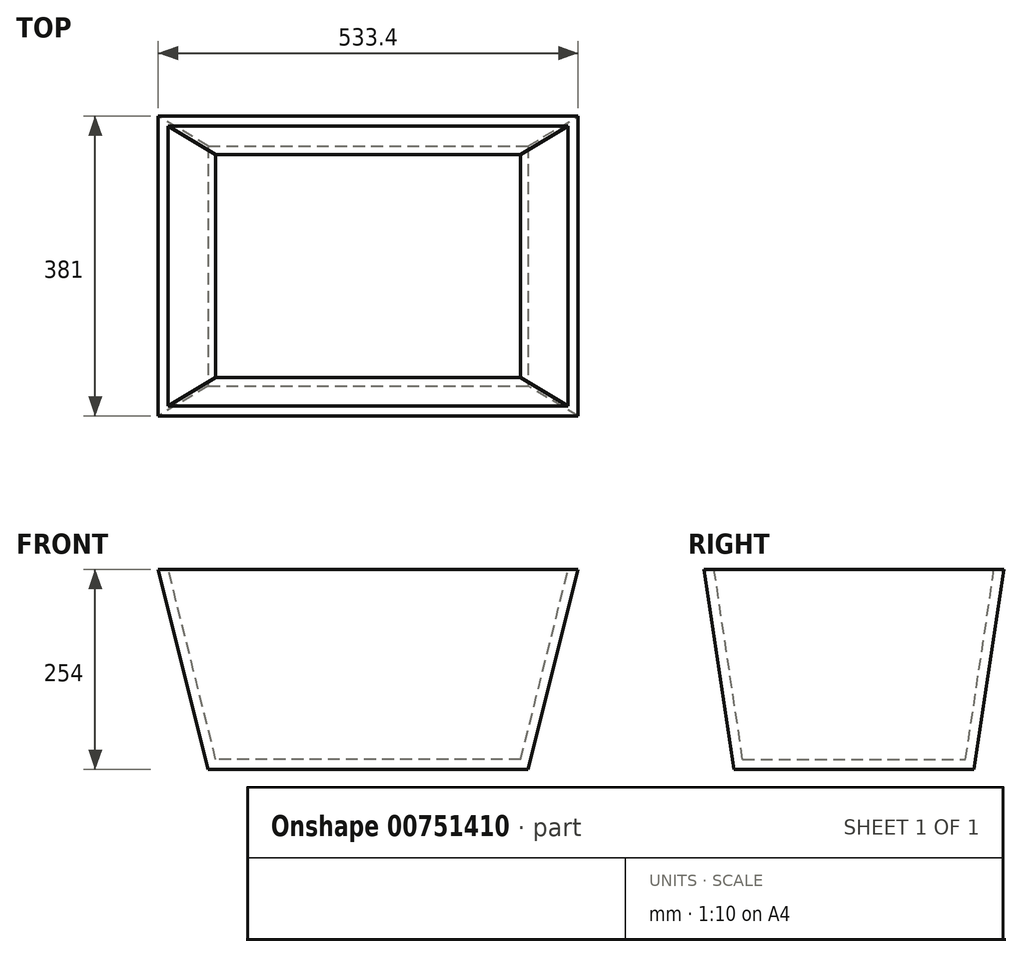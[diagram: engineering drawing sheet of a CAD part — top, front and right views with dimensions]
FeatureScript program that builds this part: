
annotation { "Feature Type Name" : "Feature", "Feature Type Description" : "" }
export const myFeature = defineFeature(function(context is Context, id is Id, definition is map)
    precondition{}
    {
        {
            var Q0;
            Q0=qCreatedBy(makeId("Top.planeOp"),FACE);
            var sketch = newSketch(context, id + "F0", { "sketchPlane" : qUnion([Q0])});
            skLineSegment(sketch, "E0.bottom", {"start": v(-203.2, 152.4) * mm, "end": v(203.2, 152.4) * mm});
            skLineSegment(sketch, "E0.top", {"start": v(-203.2, -152.4) * mm, "end": v(203.2, -152.4) * mm});
            skLineSegment(sketch, "E0.left", {"start": v(-203.2, 152.4) * mm, "end": v(-203.2, -152.4) * mm});
            skLineSegment(sketch, "E0.right", {"start": v(203.2, 152.4) * mm, "end": v(203.2, -152.4) * mm});
            skLineSegment(sketch, "E1", {"start": v(-203.2, 152.4) * mm, "end": v(203.2, -152.4) * mm, "construction": true});
            skLineSegment(sketch, "E2", {"start": v(203.2, 152.4) * mm, "end": v(-203.2, -152.4) * mm, "construction": true});
            skPoint(sketch, "E3", {"position": v(0, 0) * mm});
            skLineSegment(sketch, "E4.0", {"start": v(-190.5, 139.7) * mm, "end": v(190.5, 139.7) * mm});
            skLineSegment(sketch, "E4.1", {"start": v(-190.5, 139.7) * mm, "end": v(-190.5, -139.7) * mm});
            skLineSegment(sketch, "E4.2", {"start": v(-190.5, -139.7) * mm, "end": v(190.5, -139.7) * mm});
            skLineSegment(sketch, "E4.3", {"start": v(190.5, 139.7) * mm, "end": v(190.5, -139.7) * mm});
            skLineSegment(sketch, "E5", {"start": v(-190.5, 139.7) * mm, "end": v(-203.2, 152.4) * mm});
            skLineSegment(sketch, "E6", {"start": v(190.5, 139.7) * mm, "end": v(203.2, 152.4) * mm});
            skLineSegment(sketch, "E7", {"start": v(203.2, -152.4) * mm, "end": v(190.5, -139.7) * mm});
            skLineSegment(sketch, "E8", {"start": v(-190.5, -139.7) * mm, "end": v(-203.2, -152.4) * mm});
            skSolve(sketch);
        }
        {
            var Q0;
            Q0=qCreatedBy(makeId("Top.planeOp"),FACE);
            cPlane(context, id + "F1", {"entities" : qUnion([Q0]), "cplaneType" : CPlaneType.OFFSET, "offset" : 254 * mm, "width" : 152.4 * mm, "height" : 152.4 * mm});
        }
        {
            var Q0;
            Q0=qCreatedBy(id+"F1.planeOp",FACE);
            var sketch = newSketch(context, id + "F2", { "sketchPlane" : qUnion([Q0])});
            skLineSegment(sketch, "E9.bottom", {"start": v(-266.7, 190.5) * mm, "end": v(266.7, 190.5) * mm});
            skLineSegment(sketch, "E9.top", {"start": v(-266.7, -190.5) * mm, "end": v(266.7, -190.5) * mm});
            skLineSegment(sketch, "E9.left", {"start": v(-266.7, 190.5) * mm, "end": v(-266.7, -190.5) * mm});
            skLineSegment(sketch, "E9.right", {"start": v(266.7, 190.5) * mm, "end": v(266.7, -190.5) * mm});
            skLineSegment(sketch, "E10", {"start": v(-266.7, 190.5) * mm, "end": v(266.7, -190.5) * mm, "construction": true});
            skLineSegment(sketch, "E11", {"start": v(266.7, 190.5) * mm, "end": v(-266.7, -190.5) * mm, "construction": true});
            skPoint(sketch, "E12", {"position": v(0, 0) * mm});
            skLineSegment(sketch, "E13.0", {"start": v(-254, 177.8) * mm, "end": v(254, 177.8) * mm});
            skLineSegment(sketch, "E13.1", {"start": v(-254, 177.8) * mm, "end": v(-254, -177.8) * mm});
            skLineSegment(sketch, "E13.2", {"start": v(-254, -177.8) * mm, "end": v(254, -177.8) * mm});
            skLineSegment(sketch, "E13.3", {"start": v(254, 177.8) * mm, "end": v(254, -177.8) * mm});
            skLineSegment(sketch, "E14", {"start": v(-254, 177.8) * mm, "end": v(-266.7, 190.5) * mm});
            skLineSegment(sketch, "E15", {"start": v(254, 177.8) * mm, "end": v(266.7, 190.5) * mm});
            skLineSegment(sketch, "E16", {"start": v(266.7, -190.5) * mm, "end": v(254, -177.8) * mm});
            skLineSegment(sketch, "E17", {"start": v(-254, -177.8) * mm, "end": v(-266.7, -190.5) * mm});
            skSolve(sketch);
        }
        {
            var Q0;
            Q0=makeQuery(id+"F0.imprint","IMPRINT",FACE,{"disambiguationData":[TD([[makeQuery(id+"F0.imprint","IMPRINT",EDGE,{"derivedFrom":sQuery(id+"F0.wireOp",EDGE,"E0.bottom")}),-1.0]])]});
            var Q1;
            Q1=makeQuery(id+"F2.imprint","IMPRINT",FACE,{"disambiguationData":[TD([[makeQuery(id+"F2.imprint","IMPRINT",EDGE,{"derivedFrom":sQuery(id+"F2.wireOp",EDGE,"E9.bottom")}),-1.0]])]});
            loft(context, id + "F3", {"sheetProfilesArray" : [{ "sheetProfileEntities" : qUnion([Q0]) }, { "sheetProfileEntities" : qUnion([Q1]) }]});
        }
        {
            var Q1;
            Q1=makeQuery(id+"F0.imprint","IMPRINT",FACE,{"disambiguationData":[TD([[makeQuery(id+"F0.imprint","IMPRINT",EDGE,{"derivedFrom":sQuery(id+"F0.wireOp",EDGE,"E0.left")}),1.0]])]});
            var Q2;
            Q2=makeQuery(id+"F2.imprint","IMPRINT",FACE,{"disambiguationData":[TD([[makeQuery(id+"F2.imprint","IMPRINT",EDGE,{"derivedFrom":sQuery(id+"F2.wireOp",EDGE,"E9.left")}),1.0]])]});
            loft(context, id + "F4", {"operationType" : NewBodyOperationType.ADD, "sheetProfilesArray" : [{ "sheetProfileEntities" : qUnion([Q1]) }, { "sheetProfileEntities" : qUnion([Q2]) }]});
        }
        {
            var Q1;
            Q1=makeQuery(id+"F2.imprint","IMPRINT",FACE,{"disambiguationData":[TD([[makeQuery(id+"F2.imprint","IMPRINT",EDGE,{"derivedFrom":sQuery(id+"F2.wireOp",EDGE,"E9.top")}),1.0]])]});
            var Q2;
            Q2=makeQuery(id+"F0.imprint","IMPRINT",FACE,{"disambiguationData":[TD([[makeQuery(id+"F0.imprint","IMPRINT",EDGE,{"derivedFrom":sQuery(id+"F0.wireOp",EDGE,"E0.top")}),1.0]])]});
            loft(context, id + "F5", {"operationType" : NewBodyOperationType.ADD, "sheetProfilesArray" : [{ "sheetProfileEntities" : qUnion([Q1]) }, { "sheetProfileEntities" : qUnion([Q2]) }]});
        }
        {
            var Q1;
            Q1=makeQuery(id+"F2.imprint","IMPRINT",FACE,{"disambiguationData":[TD([[makeQuery(id+"F2.imprint","IMPRINT",EDGE,{"derivedFrom":sQuery(id+"F2.wireOp",EDGE,"E9.right")}),-1.0]])]});
            var Q2;
            Q2=makeQuery(id+"F0.imprint","IMPRINT",FACE,{"disambiguationData":[TD([[makeQuery(id+"F0.imprint","IMPRINT",EDGE,{"derivedFrom":sQuery(id+"F0.wireOp",EDGE,"E0.right")}),-1.0]])]});
            loft(context, id + "F6", {"operationType" : NewBodyOperationType.ADD, "sheetProfilesArray" : [{ "sheetProfileEntities" : qUnion([Q1]) }, { "sheetProfileEntities" : qUnion([Q2]) }]});
        }
        {
            var Q0;
            Q0=makeQuery(id+"F0.imprint","IMPRINT",FACE,{"disambiguationData":[TD([[makeQuery(id+"F0.imprint","IMPRINT",EDGE,{"derivedFrom":sQuery(id+"F0.wireOp",EDGE,"E0.bottom")}),-1.0]])]});
            var Q1;
            Q1=makeQuery(id+"F0.imprint","IMPRINT",FACE,{"disambiguationData":[TD([[makeQuery(id+"F0.imprint","IMPRINT",EDGE,{"derivedFrom":sQuery(id+"F0.wireOp",EDGE,"E0.left")}),1.0]])]});
            var Q2;
            Q2=makeQuery(id+"F0.imprint","IMPRINT",FACE,{"disambiguationData":[TD([[makeQuery(id+"F0.imprint","IMPRINT",EDGE,{"derivedFrom":sQuery(id+"F0.wireOp",EDGE,"E0.top")}),1.0]])]});
            var Q3;
            Q3=makeQuery(id+"F0.imprint","IMPRINT",FACE,{"disambiguationData":[TD([[makeQuery(id+"F0.imprint","IMPRINT",EDGE,{"derivedFrom":sQuery(id+"F0.wireOp",EDGE,"E0.right")}),-1.0]])]});
            var Q4;
            Q4=makeQuery(id+"F0.imprint","IMPRINT",FACE,{"disambiguationData":[TD([[makeQuery(id+"F0.imprint","IMPRINT",EDGE,{"derivedFrom":sQuery(id+"F0.wireOp",EDGE,"E4.0")}),-1.0]])]});
            extrude(context, id + "F7", {"entities" : qUnion([Q0, Q1, Q2, Q3, Q4]), "operationType" : NewBodyOperationType.ADD, "depth" : 12.7 * mm, "offsetDistance" : 25.4 * mm});
        }
    });
